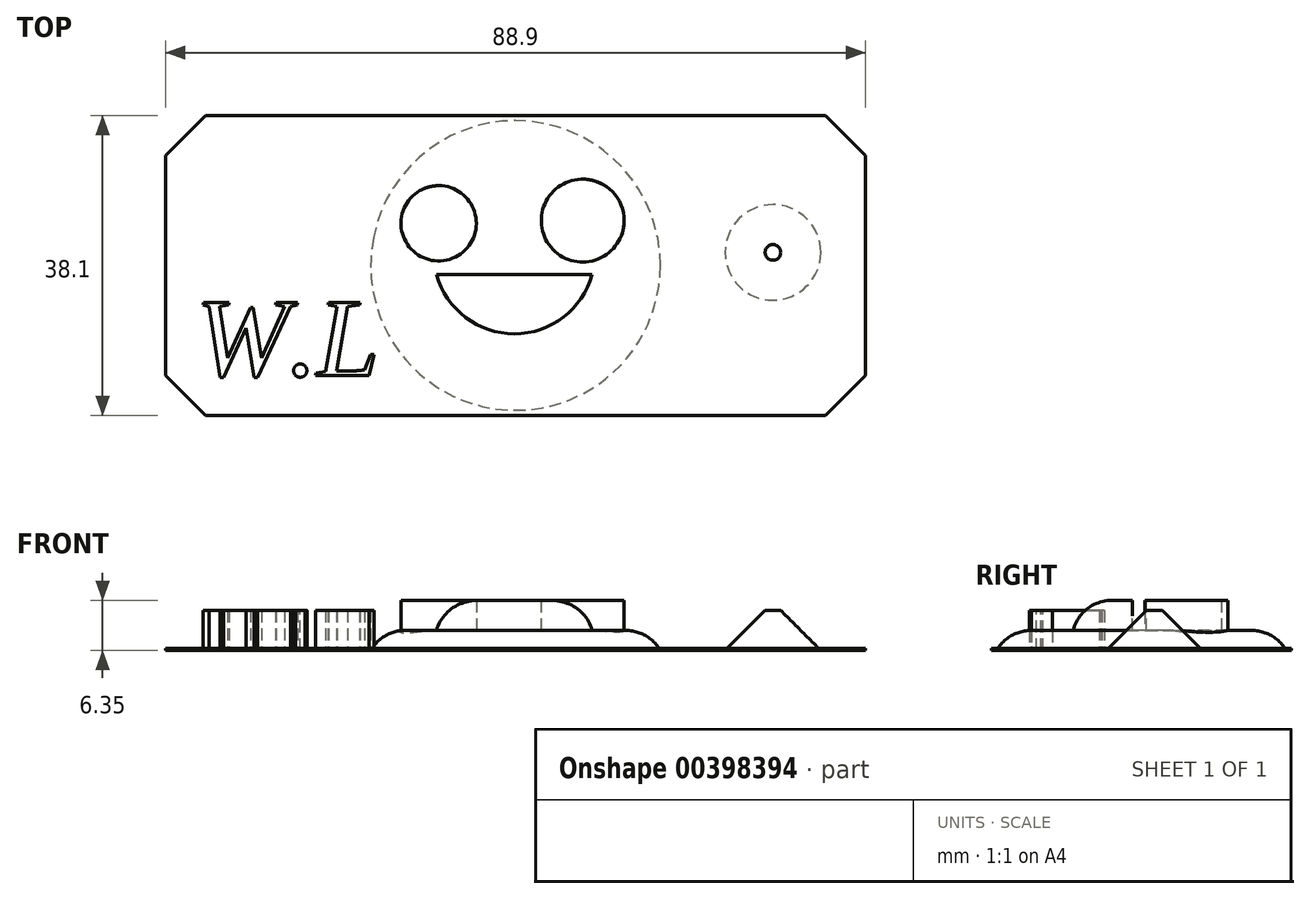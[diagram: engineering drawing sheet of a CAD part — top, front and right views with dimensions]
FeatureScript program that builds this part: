
annotation { "Feature Type Name" : "Feature", "Feature Type Description" : "" }
export const myFeature = defineFeature(function(context is Context, id is Id, definition is map)
    precondition{}
    {
        {
            var Q0;
            Q0=qCreatedBy(makeId("Top.planeOp"),FACE);
            var sketch = newSketch(context, id + "F0", { "sketchPlane" : qUnion([Q0])});
            skLineSegment(sketch, "E0.bottom", {"start": v(44.45, -19.05) * mm, "end": v(-44.45, -19.05) * mm});
            skLineSegment(sketch, "E0.top", {"start": v(44.45, 19.05) * mm, "end": v(-44.45, 19.05) * mm});
            skLineSegment(sketch, "E0.left", {"start": v(44.45, -19.05) * mm, "end": v(44.45, 19.05) * mm});
            skLineSegment(sketch, "E0.right", {"start": v(-44.45, -19.05) * mm, "end": v(-44.45, 19.05) * mm});
            skPoint(sketch, "E0.middle", {"position": v(0, 0) * mm});
            skSolve(sketch);
        }
        {
            var Q0;
            Q0=makeQuery(id+"F0.imprint","IMPRINT",FACE,{"disambiguationData":[TD([[makeQuery(id+"F0.imprint","IMPRINT",EDGE,{"derivedFrom":sQuery(id+"F0.wireOp",EDGE,"E0.bottom")}),-1.0]])]});
            var sketch = newSketch(context, id + "F1", { "sketchPlane" : qUnion([Q0])});
            skCircle(sketch, "E1", {"center": v(0, 0) * mm, "radius": 18.4 * mm});
            skSolve(sketch);
        }
        {
            var Q0;
            Q0=makeQuery(id+"F1.imprint","IMPRINT",FACE,{"disambiguationData":[TD([[makeQuery(id+"F1.imprint","IMPRINT",EDGE,{"derivedFrom":sQuery(id+"F1.wireOp",EDGE,"E1")}),1.0]])]});
            var Q1;
            Q1=sQuery(id+"F1.wireOp",EDGE,"E1");
            extrude(context, id + "F2", {"entities" : qUnion([Q0]), "surfaceEntities" : qUnion([Q1]), "depth" : 2.54 * mm});
        }
        {
            var Q0;
            Q0=makeQuery(id+"F2.opExtrude","CAP_FACE",FACE,{"disambiguationData":[OSD([sQuery(id+"F1.wireOp",EDGE,"E1")])],"isStart":false});
            var sketch = newSketch(context, id + "F3", { "sketchPlane" : qUnion([Q0])});
            skCircle(sketch, "E2", {"center": v(-9.77, 5.36) * mm, "radius": 4.78 * mm});
            skSolve(sketch);
        }
        {
            var Q0;
            Q0=makeQuery(id+"F3.imprint","IMPRINT",FACE,{"disambiguationData":[TD([[makeQuery(id+"F3.imprint","IMPRINT",EDGE,{"derivedFrom":sQuery(id+"F3.wireOp",EDGE,"E2")}),1.0]])]});
            extrude(context, id + "F4", {"entities" : qUnion([Q0]), "operationType" : NewBodyOperationType.ADD, "depth" : 3.8 * mm});
        }
        {
            var Q0;
            Q0=makeQuery(id+"F2.opExtrude","CAP_FACE",FACE,{"disambiguationData":[OSD([sQuery(id+"F1.wireOp",EDGE,"E1")])],"isStart":false});
            var sketch = newSketch(context, id + "F5", { "sketchPlane" : qUnion([Q0])});
            skCircle(sketch, "E3", {"center": v(8.53, 5.7) * mm, "radius": 5.26 * mm});
            skSolve(sketch);
        }
        {
            var Q0;
            Q0=makeQuery(id+"F5.imprint","IMPRINT",FACE,{"disambiguationData":[TD([[makeQuery(id+"F5.imprint","IMPRINT",EDGE,{"derivedFrom":sQuery(id+"F5.wireOp",EDGE,"E3")}),1.0]])]});
            extrude(context, id + "F6", {"entities" : qUnion([Q0]), "operationType" : NewBodyOperationType.ADD, "depth" : 3.8 * mm});
        }
        {
            var Q0;
            Q0=makeQuery(id+"F2.opExtrude","CAP_FACE",FACE,{"disambiguationData":[OSD([sQuery(id+"F1.wireOp",EDGE,"E1")])],"isStart":false});
            var sketch = newSketch(context, id + "F7", { "sketchPlane" : qUnion([Q0])});
            skArc(sketch, "E4", {"start": v(-10.03, -1.17) * mm, "mid": v(-0.14, -8.68) * mm, "end": v(9.74, -1.15) * mm});
            skLineSegment(sketch, "E5", {"start": v(-10.03, -1.17) * mm, "end": v(9.74, -1.15) * mm});
            skSolve(sketch);
        }
        {
            var Q0;
            Q0=makeQuery(id+"F7.imprint","IMPRINT",FACE,{"disambiguationData":[TD([[makeQuery(id+"F7.imprint","IMPRINT",EDGE,{"derivedFrom":sQuery(id+"F7.wireOp",EDGE,"E4")}),1.0]])]});
            extrude(context, id + "F8", {"entities" : qUnion([Q0]), "operationType" : NewBodyOperationType.ADD, "depth" : 3.8 * mm});
        }
        {
            var Q0;
            Q0=makeQuery(id+"F0.imprint","IMPRINT",FACE,{"disambiguationData":[TD([[makeQuery(id+"F0.imprint","IMPRINT",EDGE,{"derivedFrom":sQuery(id+"F0.wireOp",EDGE,"E0.bottom")}),-1.0]])]});
            var Q1;
            Q1=sQuery(id+"F0.wireOp",EDGE,"E0.right");
            var Q2;
            Q2=sQuery(id+"F0.wireOp",EDGE,"E0.top");
            var Q3;
            Q3=sQuery(id+"F0.wireOp",EDGE,"E0.bottom");
            var Q4;
            Q4=sQuery(id+"F0.wireOp",EDGE,"E0.left");
            extrude(context, id + "F9", {"entities" : qUnion([Q0]), "bodyType" : ToolBodyType.SURFACE, "surfaceEntities" : qUnion([Q1, Q2, Q3, Q4]), "depth" : 6.35 * mm});
        }
        {
            var Q0;
            Q0=makeQuery(id+"F1.imprint","IMPRINT",FACE,{"disambiguationData":[TD([[makeQuery(id+"F1.imprint","IMPRINT",EDGE,{"derivedFrom":sQuery(id+"F1.wireOp",EDGE,"E1")}),-1.0]])]});
            var sketch = newSketch(context, id + "F10", { "sketchPlane" : qUnion([Q0])});
            skLineSegment(sketch, "E6.bottom", {"start": v(-44.48, -19.03) * mm, "end": v(44.25, -19.03) * mm});
            skLineSegment(sketch, "E6.top", {"start": v(-44.48, 19.03) * mm, "end": v(44.25, 19.03) * mm});
            skLineSegment(sketch, "E6.left", {"start": v(-44.48, -19.03) * mm, "end": v(-44.48, 19.03) * mm});
            skLineSegment(sketch, "E6.right", {"start": v(44.25, -19.03) * mm, "end": v(44.25, 19.03) * mm});
            skSolve(sketch);
        }
        {
            var Q0;
            {var subQ0=sQuery(id+"F10.wireOp",EDGE,"E6.right");Q0=makeQuery(id+"F10.imprint","IMPRINT",FACE,{"disambiguationData":[TD([[makeQuery(id+"F10.imprint","IMPRINT",EDGE,{"derivedFrom":subQ0}),1.0]])]});}
            var sketch = newSketch(context, id + "F11", { "sketchPlane" : qUnion([Q0])});
            skCircle(sketch, "E7", {"center": v(32.7, 1.65) * mm, "radius": 6.07 * mm});
            skPoint(sketch, "E7.first.point", {"position": v(26.85, 0) * mm});
            skPoint(sketch, "E7.second.point", {"position": v(35.41, 7.08) * mm});
            skPoint(sketch, "E7.third.point", {"position": v(37.34, -2.25) * mm});
            skCircle(sketch, "E8", {"center": v(-29.6, -0.33) * mm, "radius": 6.56 * mm});
            skPoint(sketch, "E8.first.point", {"position": v(-27.88, 6) * mm});
            skPoint(sketch, "E8.second.point", {"position": v(-30.96, -6.75) * mm});
            skPoint(sketch, "E8.third.point", {"position": v(-36.16, 0) * mm});
            skSolve(sketch);
        }
        {
            var Q0;
            Q0=makeQuery(id+"F11.imprint","IMPRINT",FACE,{"disambiguationData":[TD([[makeQuery(id+"F11.imprint","IMPRINT",EDGE,{"derivedFrom":sQuery(id+"F11.wireOp",EDGE,"E7")}),1.0]])]});
            var Q1;
            Q1=sQuery(id+"F11.wireOp",EDGE,"E8");
            var Q2;
            Q2=sQuery(id+"F11.wireOp",EDGE,"E7");
            extrude(context, id + "F12", {"entities" : qUnion([Q0]), "surfaceEntities" : qUnion([Q1, Q2]), "depth" : 5.08 * mm});
        }
        {
            var Q0;
            {var subQ0=sQuery(id+"F10.wireOp",EDGE,"E6.right");Q0=makeQuery(id+"F10.imprint","IMPRINT",FACE,{"disambiguationData":[TD([[makeQuery(id+"F10.imprint","IMPRINT",EDGE,{"derivedFrom":subQ0}),1.0]])]});}
            var sketch = newSketch(context, id + "F13", { "sketchPlane" : qUnion([Q0])});
            skSolve(sketch);
        }
        {
            var Q0;
            {var subQ0=sQuery(id+"F10.wireOp",EDGE,"E6.right");Q0=makeQuery(id+"F13.imprint","IMPRINT",FACE,{"disambiguationData":[TD([[makeQuery(id+"F13.imprint","IMPRINT",EDGE,{"derivedFrom":makeQuery(id+"F10.imprint","IMPRINT",EDGE,{"derivedFrom":subQ0})}),1.0]])]});}
            var sketch = newSketch(context, id + "F14", { "sketchPlane" : qUnion([Q0])});
            skText(sketch, "E9", { "text": "W.L", "fontName": "Tinos-Italic.ttf"});
            const initialGuessF14  = {"E9": [-0.04064, -0.014, 1, 0, 0.01025]};
            skSetInitialGuess(sketch, initialGuessF14);
            skSolve(sketch);
        }
        {
            var Q0;
            Q0 = qSketchRegion(id + "F14", true);
            extrude(context, id + "F15", {"entities" : qUnion([Q0]), "depth" : 5.08 * mm});
        }
        {
            var Q0;
            Q0=makeQuery(id+"F9.opExtrude","SWEPT_FACE",FACE,{"disambiguationData":[OSD([sQuery(id+"F0.wireOp",EDGE,"E0.right")])]});
            var Q1;
            Q1=makeQuery(id+"F9.opExtrude","SWEPT_FACE",FACE,{"disambiguationData":[OSD([sQuery(id+"F0.wireOp",EDGE,"E0.left")])]});
            var Q2;
            Q2=makeQuery(id+"F9.opExtrude","SWEPT_FACE",FACE,{"disambiguationData":[OSD([sQuery(id+"F0.wireOp",EDGE,"E0.bottom")])]});
            var Q3;
            Q3=makeQuery(id+"F9.opExtrude","SWEPT_FACE",FACE,{"disambiguationData":[OSD([sQuery(id+"F0.wireOp",EDGE,"E0.top")])]});
            chamfer(context, id + "F16", {"entities" : qUnion([Q0, Q1, Q2, Q3]), "width" : 5.08 * mm, "tangentPropagation" : true});
        }
        {
            var Q0;
            Q0=makeQuery(id+"F2.opExtrude","CAP_EDGE",EDGE,{"disambiguationData":[OSD([sQuery(id+"F1.wireOp",EDGE,"E1")])],"isStart":false});
            var Q1;
            Q1=makeQuery(id+"F8.opExtrude","CAP_EDGE",EDGE,{"disambiguationData":[OSD([sQuery(id+"F7.wireOp",EDGE,"E4")])],"isStart":false});
            fillet(context, id + "F17", {"entities" : qUnion([Q0, Q1]), "radius" : 5.08 * mm, "tangentPropagation" : true, "allowEdgeOverflow" : false});
        }
        {
            var Q0;
            Q0=makeQuery(id+"F12.opExtrude","CAP_FACE",FACE,{"disambiguationData":[OSD([sQuery(id+"F11.wireOp",EDGE,"E7")])],"isStart":false});
            chamfer(context, id + "F18", {"entities" : qUnion([Q0]), "width" : 5.08 * mm, "tangentPropagation" : true});
        }
        {
            var Q0;
            Q0=makeQuery(id+"F0.imprint","IMPRINT",FACE,{"disambiguationData":[TD([[makeQuery(id+"F0.imprint","IMPRINT",EDGE,{"derivedFrom":sQuery(id+"F0.wireOp",EDGE,"E0.bottom")}),-1.0]])]});
            extrude(context, id + "F19", {"entities" : qUnion([Q0]), "depth" : 0.25 * mm});
        }
        {
            var Q0;
            Q0=makeQuery(id+"F19.opExtrude","SWEPT_EDGE",EDGE,{"disambiguationData":[OSD([sQuery(id+"F0.wireOp",EDGE,"E0.bottom"),sQuery(id+"F0.wireOp",EDGE,"E0.left")])]});
            var Q1;
            Q1=makeQuery(id+"F19.opExtrude","SWEPT_EDGE",EDGE,{"disambiguationData":[OSD([sQuery(id+"F0.wireOp",EDGE,"E0.top"),sQuery(id+"F0.wireOp",EDGE,"E0.left")])]});
            var Q2;
            Q2=makeQuery(id+"F19.opExtrude","SWEPT_EDGE",EDGE,{"disambiguationData":[OSD([sQuery(id+"F0.wireOp",EDGE,"E0.bottom"),sQuery(id+"F0.wireOp",EDGE,"E0.right")])]});
            var Q3;
            Q3=makeQuery(id+"F19.opExtrude","SWEPT_EDGE",EDGE,{"disambiguationData":[OSD([sQuery(id+"F0.wireOp",EDGE,"E0.top"),sQuery(id+"F0.wireOp",EDGE,"E0.right")])]});
            chamfer(context, id + "F20", {"entities" : qUnion([Q0, Q1, Q2, Q3]), "width" : 5.08 * mm, "tangentPropagation" : true});
        }
    });
